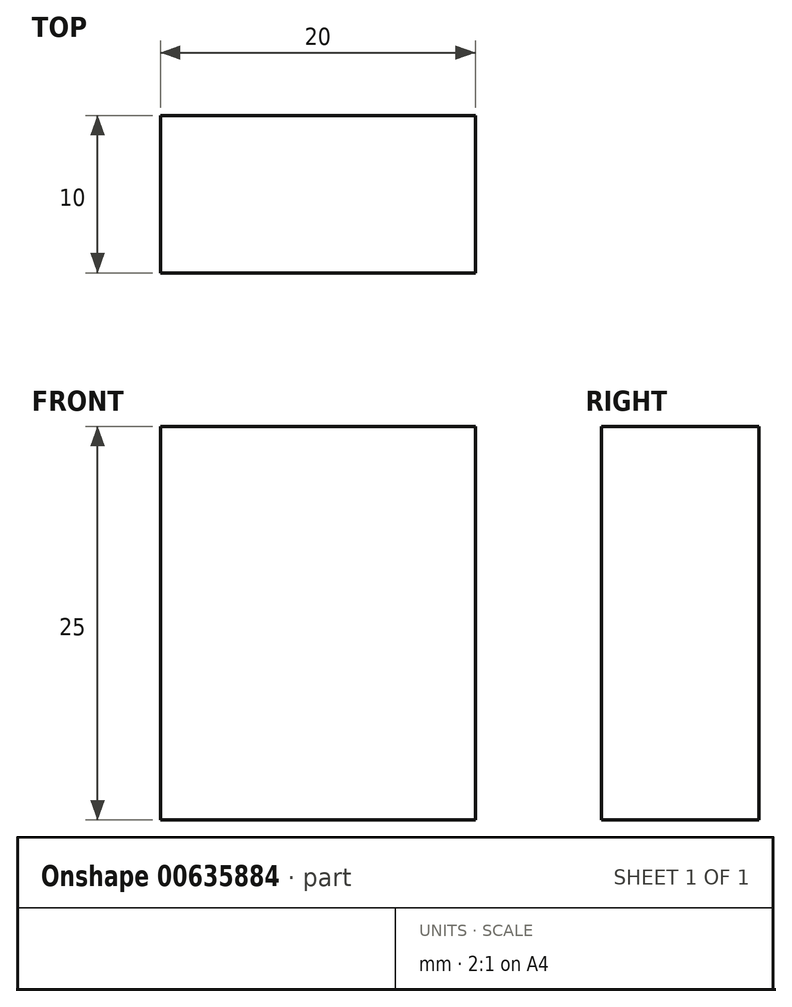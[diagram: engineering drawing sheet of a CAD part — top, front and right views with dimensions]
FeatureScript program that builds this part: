
annotation { "Feature Type Name" : "Feature", "Feature Type Description" : "" }
export const myFeature = defineFeature(function(context is Context, id is Id, definition is map)
    precondition{}
    {
        {
            var Q0;
            Q0=qCreatedBy(makeId("Top.planeOp"),FACE);
            var sketch = newSketch(context, id + "F0", { "sketchPlane" : qUnion([Q0])});
            skLineSegment(sketch, "E0.bottom", {"start": v(0, 0) * mm, "end": v(20, 0) * mm});
            skLineSegment(sketch, "E0.top", {"start": v(0, 10) * mm, "end": v(20, 10) * mm});
            skLineSegment(sketch, "E0.left", {"start": v(0, 0) * mm, "end": v(0, 10) * mm});
            skLineSegment(sketch, "E0.right", {"start": v(20, 0) * mm, "end": v(20, 10) * mm});
            skSolve(sketch);
        }
        {
            var Q0;
            Q0 = qSketchRegion(id + "F0", true);
            extrude(context, id + "F1", {"entities" : qUnion([Q0]), "depth" : 25 * mm, "offsetDistance" : 25 * mm});
        }
    });
